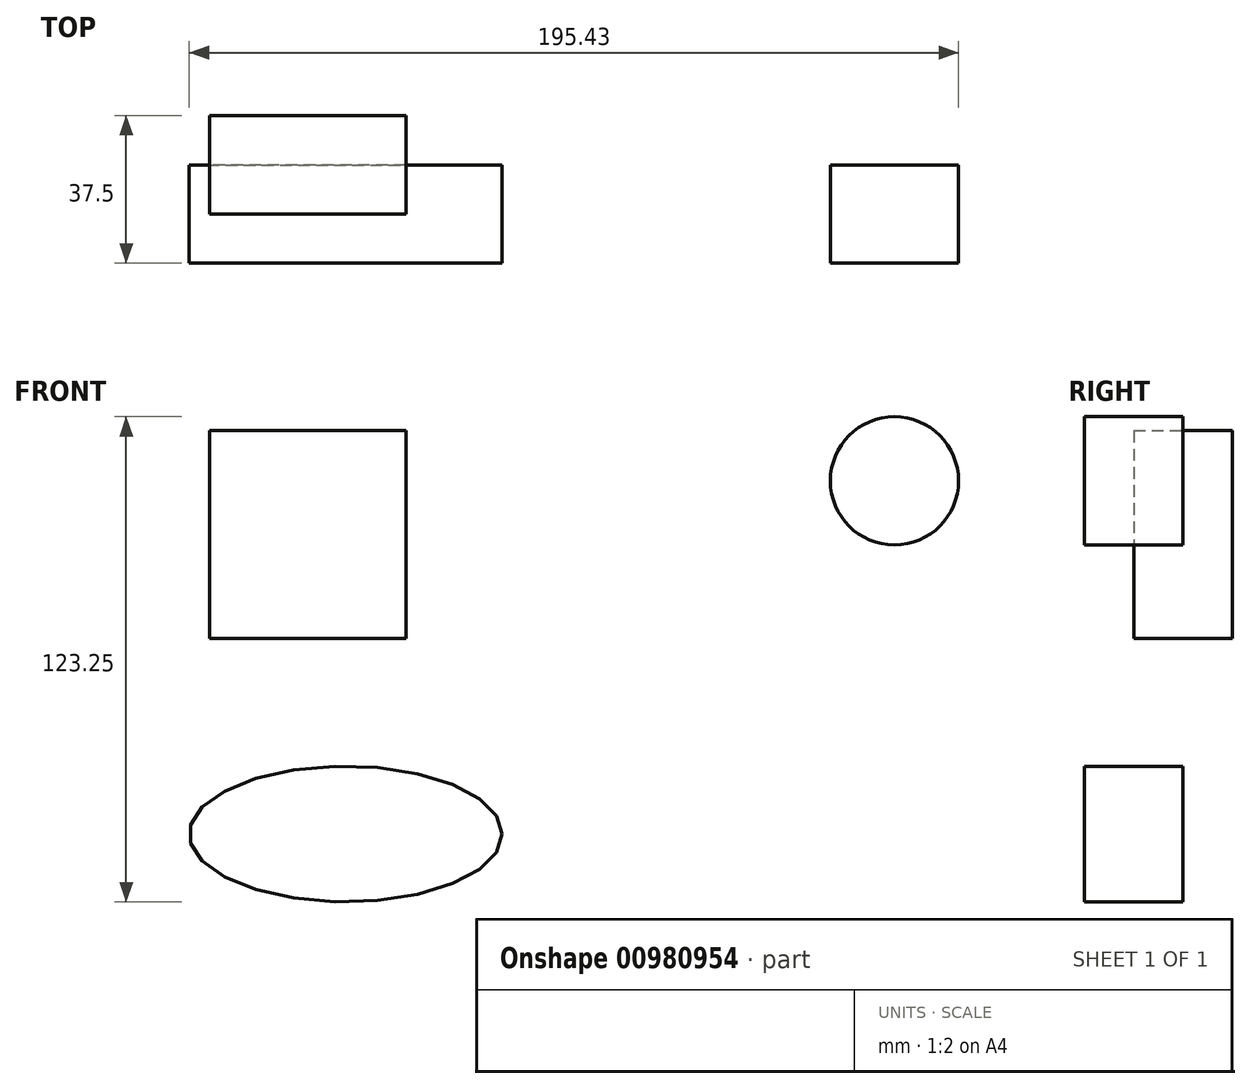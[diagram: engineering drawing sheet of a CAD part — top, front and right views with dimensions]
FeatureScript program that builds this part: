
annotation { "Feature Type Name" : "Feature", "Feature Type Description" : "" }
export const myFeature = defineFeature(function(context is Context, id is Id, definition is map)
    precondition{}
    {
        {
            var Q0;
            Q0=qCreatedBy(makeId("Front.planeOp"),FACE);
            var sketch = newSketch(context, id + "F0", { "sketchPlane" : qUnion([Q0])});
            skLineSegment(sketch, "E0.bottom", {"start": v(-49.88, 61.33) * mm, "end": v(0, 61.33) * mm});
            skLineSegment(sketch, "E0.top", {"start": v(-49.88, 8.56) * mm, "end": v(0, 8.56) * mm});
            skLineSegment(sketch, "E0.left", {"start": v(-49.88, 61.33) * mm, "end": v(-49.88, 8.56) * mm});
            skLineSegment(sketch, "E0.right", {"start": v(0, 61.33) * mm, "end": v(0, 8.56) * mm});
            skSolve(sketch);
        }
        {
            var Q0;
            Q0 = qSketchRegion(id + "F0", true);
            extrude(context, id + "F1", {"entities" : qUnion([Q0]), "endBound" : BoundingType.SYMMETRIC, "depth" : 25 * mm, "offsetDistance" : 25 * mm});
        }
        {
            var Q0;
            Q0=qCreatedBy(makeId("Front.planeOp"),FACE);
            var sketch = newSketch(context, id + "F2", { "sketchPlane" : qUnion([Q0])});
            skCircle(sketch, "E1", {"center": v(124.1, 48.6) * mm, "radius": 16.28 * mm});
            skSolve(sketch);
        }
        {
            var Q0;
            Q0 = qSketchRegion(id + "F2", true);
            extrude(context, id + "F3", {"entities" : qUnion([Q0]), "depth" : 25 * mm, "offsetDistance" : 25 * mm});
        }
        {
            var Q0;
            Q0=qCreatedBy(makeId("Front.planeOp"),FACE);
            var sketch = newSketch(context, id + "F4", { "sketchPlane" : qUnion([Q0])});
            skEllipse(sketch, "E2", {"center": v(-15.31, -41.13) * mm, "majorRadius": 39.73 * mm, "minorRadius": 17.23 * mm, "majorAxis": v(1, 0)});
            skSolve(sketch);
        }
        {
            var Q0;
            Q0 = qSketchRegion(id + "F4", true);
            extrude(context, id + "F5", {"entities" : qUnion([Q0]), "depth" : 25 * mm, "offsetDistance" : 25 * mm});
        }
    });
